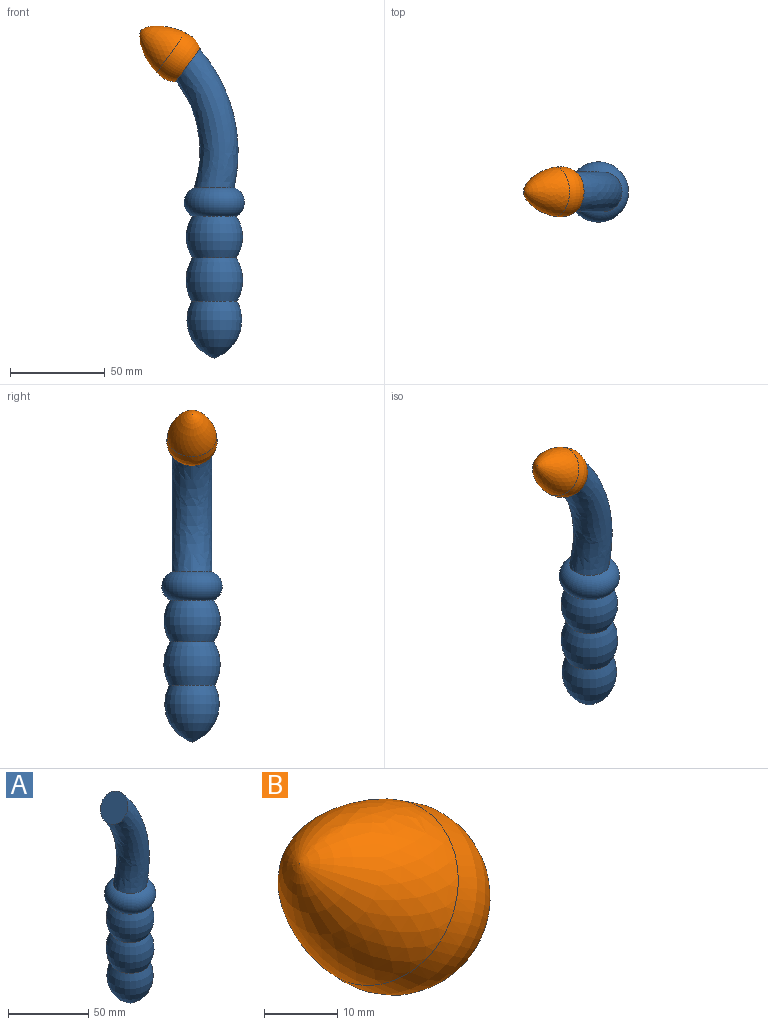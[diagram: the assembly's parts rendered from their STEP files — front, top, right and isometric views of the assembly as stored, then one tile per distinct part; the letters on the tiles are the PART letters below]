
ASSEMBLY  parts=2 mates=1
PART A: 6 faces, bbox 36.8x42x163.5 mm
  f0: torus R=7.85mm, axis (0,0,1), area 1711.3mm2, adj f1,f5
  f1: revolved ~30x30mm, area 2036.5mm2, adj f0,f2
  f2: revolved ~30x30mm, area 2114.5mm2, adj f1,f3
  f3: revolved ~30x29mm, area 2451.2mm2, adj f2
  f4: plane 21x16.99mm, normal (-0.81,0,0.59), area 346.4mm2, adj f5
  f5: bspline ~73.49x42mm, area 4486.3mm2, adj f0,f4
PART B: 3 faces, bbox 23.6x26.6x25.4 mm
  f0: plane 21.97x17.03mm, normal (0.78,0,-0.63), area 379.1mm2, adj f1
  f1: revolved ~26.64x25.44mm, area 1829.1mm2, adj f0,f2
  f2: revolved ~25.89x20.07mm, area 0mm2, adj f1
PLACE A t=(53.54,19.69,-7.03)mm
PLACE B rot(axis=(0,-1,0),3.2deg) t=(58.59,19.69,-7.61)mm
MATE fastened B.f0 <-> A.f4  axis (0.81,0,-0.59) through (39.54,19.69,57.97)mm
